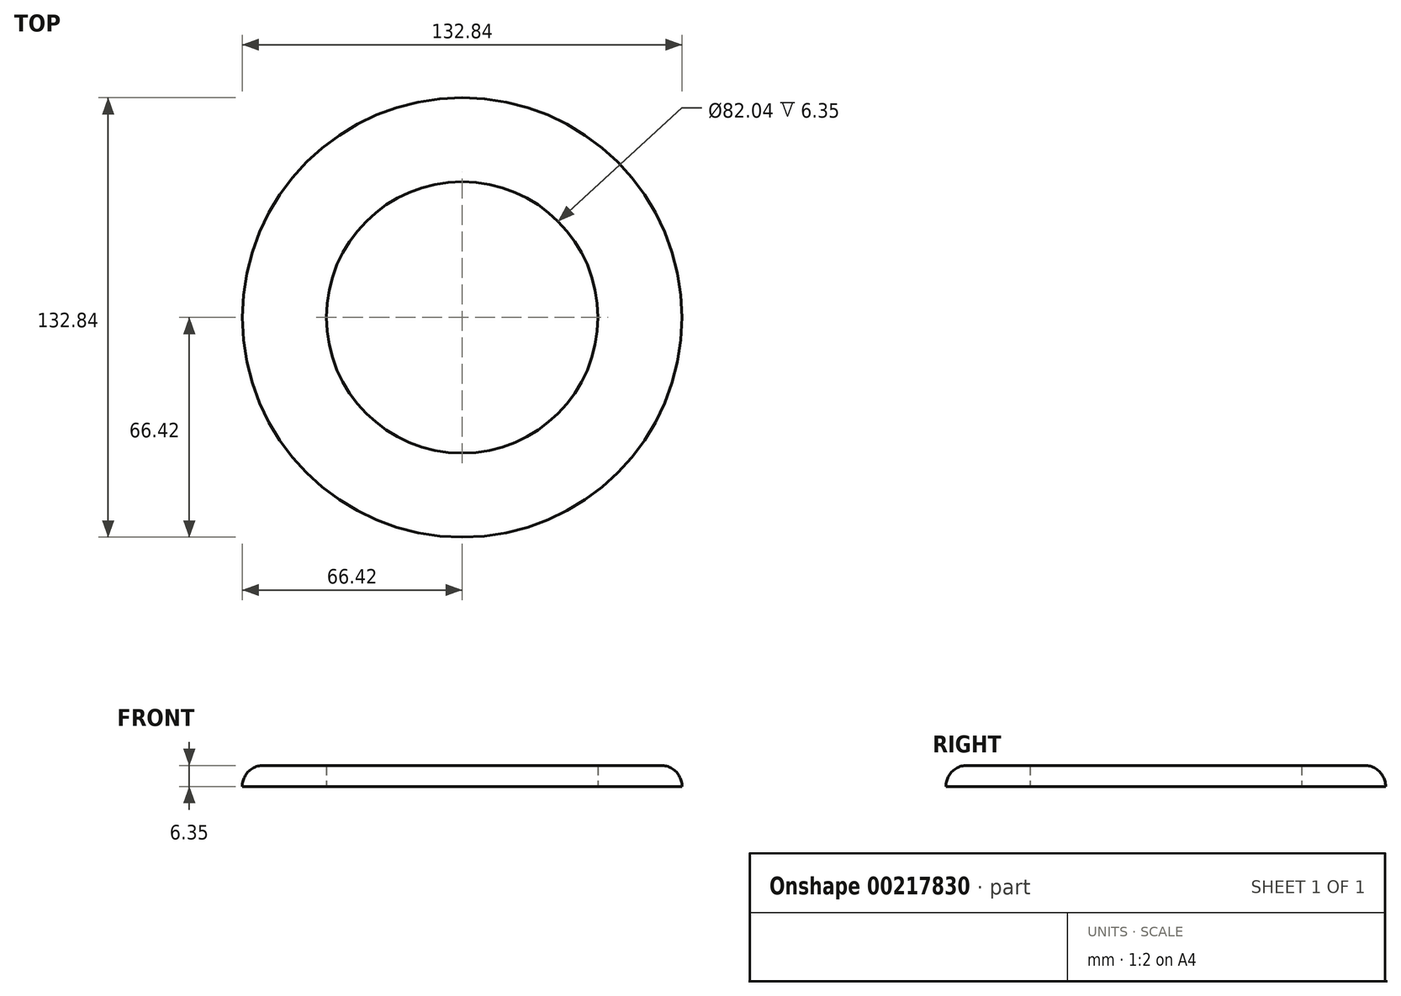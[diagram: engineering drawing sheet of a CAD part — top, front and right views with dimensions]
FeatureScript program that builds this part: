
annotation { "Feature Type Name" : "Feature", "Feature Type Description" : "" }
export const myFeature = defineFeature(function(context is Context, id is Id, definition is map)
    precondition{}
    {
        {
            var Q0;
            Q0=qCreatedBy(makeId("Top.planeOp"),FACE);
            var sketch = newSketch(context, id + "F0", { "sketchPlane" : qUnion([Q0])});
            skCircle(sketch, "E0", {"center": v(0, 0) * mm, "radius": 41.02 * mm});
            skCircle(sketch, "E1.0", {"center": v(0, 0) * mm, "radius": 66.42 * mm});
            skSolve(sketch);
        }
        {
            var Q0;
            Q0 = qSketchRegion(id + "F0", true);
            var Q1;
            Q1=makeQuery(id+"F0.imprint","IMPRINT",FACE,{"disambiguationData":[TD([[makeQuery(id+"F0.imprint","IMPRINT",EDGE,{"derivedFrom":sQuery(id+"F0.wireOp",EDGE,"E0")}),-1.0]])]});
            extrude(context, id + "F1", {"entities" : qUnion([Q0, Q1]), "depth" : 6.35 * mm});
        }
        {
            var Q0;
            Q0=makeQuery(id+"F1.opExtrude","CAP_EDGE",EDGE,{"disambiguationData":[OSD([sQuery(id+"F0.wireOp",EDGE,"E1.0")])],"isStart":false});
            fillet(context, id + "F2", {"entities" : qUnion([Q0]), "radius" : 6.35 * mm, "tangentPropagation" : true, "allowEdgeOverflow" : false});
        }
    });
